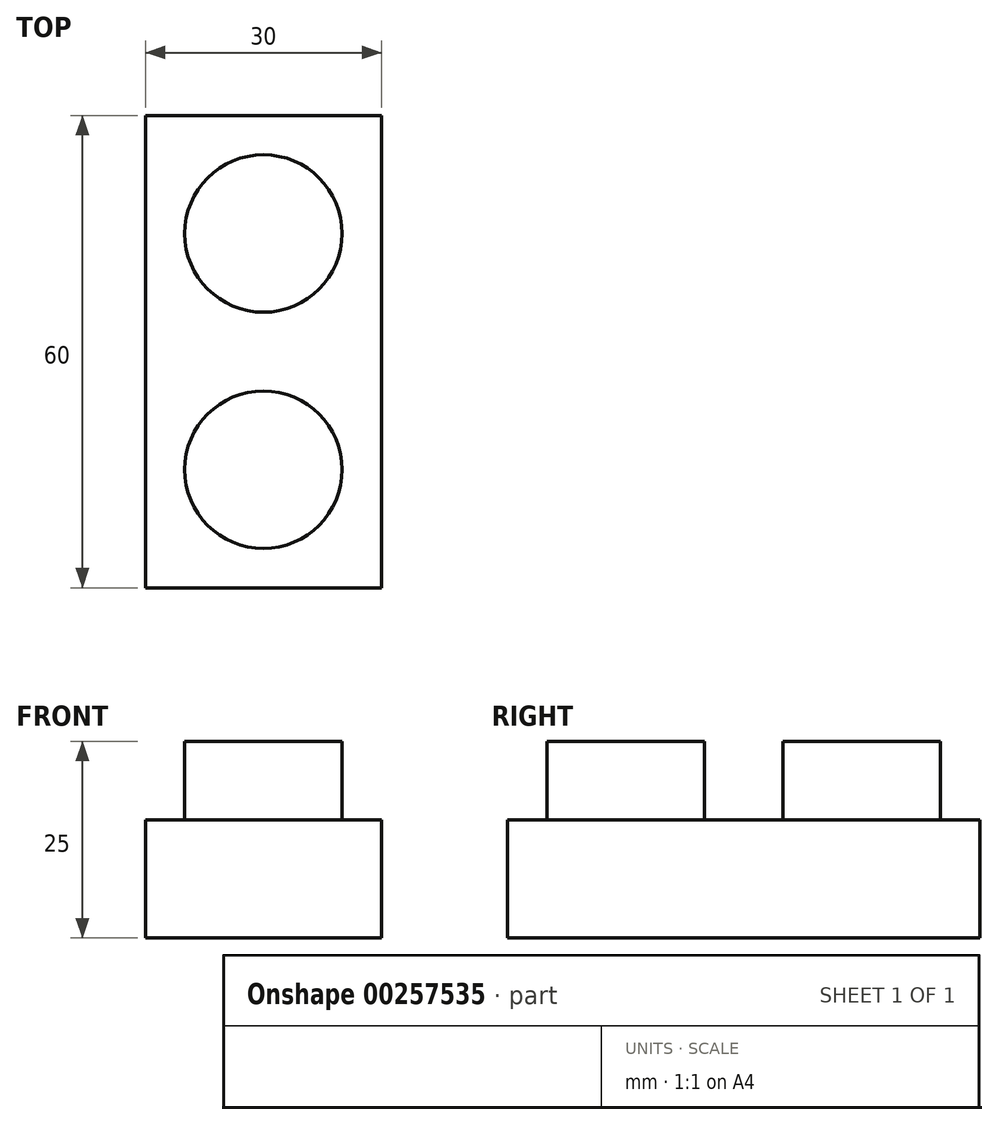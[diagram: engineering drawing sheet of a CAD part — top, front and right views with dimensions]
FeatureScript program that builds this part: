
annotation { "Feature Type Name" : "Feature", "Feature Type Description" : "" }
export const myFeature = defineFeature(function(context is Context, id is Id, definition is map)
    precondition{}
    {
        {
            var Q0;
            Q0=qCreatedBy(makeId("Top.planeOp"),FACE);
            var sketch = newSketch(context, id + "F0", { "sketchPlane" : qUnion([Q0])});
            skLineSegment(sketch, "E0.bottom", {"start": v(0, 0) * mm, "end": v(30, 0) * mm});
            skLineSegment(sketch, "E0.top", {"start": v(0, 60) * mm, "end": v(30, 60) * mm});
            skLineSegment(sketch, "E0.left", {"start": v(0, 0) * mm, "end": v(0, 60) * mm});
            skLineSegment(sketch, "E0.right", {"start": v(30, 0) * mm, "end": v(30, 60) * mm});
            skSolve(sketch);
        }
        {
            var Q0;
            Q0=qCreatedBy(makeId("Top.planeOp"),FACE);
            var sketch = newSketch(context, id + "F1", { "sketchPlane" : qUnion([Q0])});
            skLineSegment(sketch, "E1.bottom", {"start": v(0, 0) * mm, "end": v(30, 0) * mm});
            skLineSegment(sketch, "E1.top", {"start": v(0, 60) * mm, "end": v(30, 60) * mm});
            skLineSegment(sketch, "E1.left", {"start": v(0, 0) * mm, "end": v(0, 60) * mm});
            skLineSegment(sketch, "E1.right", {"start": v(30, 0) * mm, "end": v(30, 60) * mm});
            skCircle(sketch, "E2", {"center": v(15, 15) * mm, "radius": 10 * mm});
            skCircle(sketch, "E3", {"center": v(15, 45) * mm, "radius": 10 * mm});
            skSolve(sketch);
        }
        {
            var Q0;
            Q0=makeQuery(id+"F0.imprint","IMPRINT",FACE,{"disambiguationData":[TD([[makeQuery(id+"F0.imprint","IMPRINT",EDGE,{"derivedFrom":sQuery(id+"F0.wireOp",EDGE,"E0.bottom")}),1.0]])]});
            extrude(context, id + "F2", {"entities" : qUnion([Q0]), "depth" : 15 * mm});
        }
        {
            var Q0;
            Q0=makeQuery(id+"F1.imprint","IMPRINT",FACE,{"disambiguationData":[TD([[makeQuery(id+"F1.imprint","IMPRINT",EDGE,{"derivedFrom":sQuery(id+"F1.wireOp",EDGE,"E2")}),1.0]])]});
            var Q1;
            Q1=makeQuery(id+"F1.imprint","IMPRINT",FACE,{"disambiguationData":[TD([[makeQuery(id+"F1.imprint","IMPRINT",EDGE,{"derivedFrom":sQuery(id+"F1.wireOp",EDGE,"E3")}),1.0]])]});
            extrude(context, id + "F3", {"entities" : qUnion([Q0, Q1]), "operationType" : NewBodyOperationType.ADD, "depth" : 25 * mm});
        }
    });
